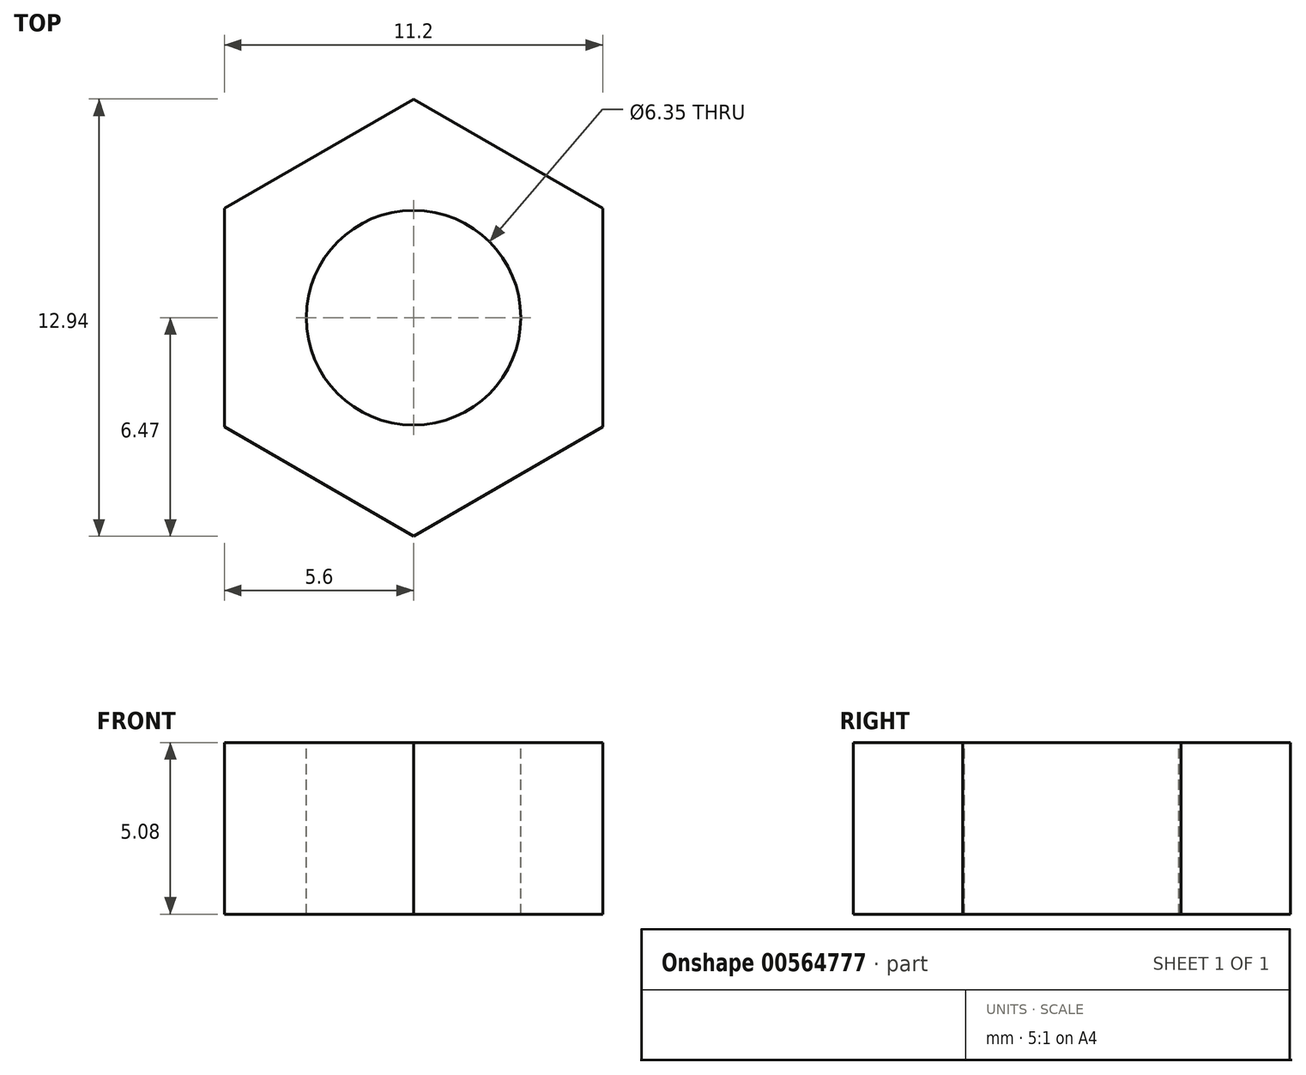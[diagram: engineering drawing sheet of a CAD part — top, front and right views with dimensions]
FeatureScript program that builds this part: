
annotation { "Feature Type Name" : "Feature", "Feature Type Description" : "" }
export const myFeature = defineFeature(function(context is Context, id is Id, definition is map)
    precondition{}
    {
        {
            var Q0;
            Q0=qCreatedBy(makeId("Top.planeOp"),FACE);
            var sketch = newSketch(context, id + "F0", { "sketchPlane" : qUnion([Q0])});
            skCircle(sketch, "E0.cCircle", {"center": v(0, 0) * mm, "radius": 5.6 * mm, "construction": true});
            skLineSegment(sketch, "E0.0", {"start": v(-5.6, -3.23) * mm, "end": v(-5.6, 3.23) * mm});
            skLineSegment(sketch, "E0.1", {"start": v(-5.6, 3.23) * mm, "end": v(0, 6.47) * mm});
            skLineSegment(sketch, "E0.2", {"start": v(0, 6.47) * mm, "end": v(5.6, 3.23) * mm});
            skLineSegment(sketch, "E0.3", {"start": v(5.6, 3.23) * mm, "end": v(5.6, -3.23) * mm});
            skLineSegment(sketch, "E0.4", {"start": v(5.6, -3.23) * mm, "end": v(0, -6.47) * mm});
            skLineSegment(sketch, "E0.5", {"start": v(0, -6.47) * mm, "end": v(-5.6, -3.23) * mm});
            skPoint(sketch, "E0.0.midPoint", {"position": v(-5.6, 0) * mm});
            skSolve(sketch);
        }
        {
            var Q0;
            Q0 = qSketchRegion(id + "F0", true);
            extrude(context, id + "F1", {"entities" : qUnion([Q0]), "depth" : 5.08 * mm, "offsetDistance" : 25 * mm});
        }
        {
            var Q0;
            Q0=makeQuery(id+"F1.opExtrude","CAP_FACE",FACE,{"disambiguationData":[OSD([sQuery(id+"F0.wireOp",EDGE,"E0.0"),sQuery(id+"F0.wireOp",EDGE,"E0.1"),sQuery(id+"F0.wireOp",EDGE,"E0.2"),sQuery(id+"F0.wireOp",EDGE,"E0.3"),sQuery(id+"F0.wireOp",EDGE,"E0.4"),sQuery(id+"F0.wireOp",EDGE,"E0.5")])],"isStart":false});
            var sketch = newSketch(context, id + "F2", { "sketchPlane" : qUnion([Q0])});
            skCircle(sketch, "E1", {"center": v(0, 0) * mm, "radius": 3.17 * mm});
            skSolve(sketch);
        }
        {
            var Q0;
            Q0 = qSketchRegion(id + "F2", true);
            extrude(context, id + "F3", {"entities" : qUnion([Q0]), "operationType" : NewBodyOperationType.REMOVE, "endBound" : BoundingType.THROUGH_ALL, "oppositeDirection" : true, "depth" : 25 * mm, "offsetDistance" : 25 * mm});
        }
    });
